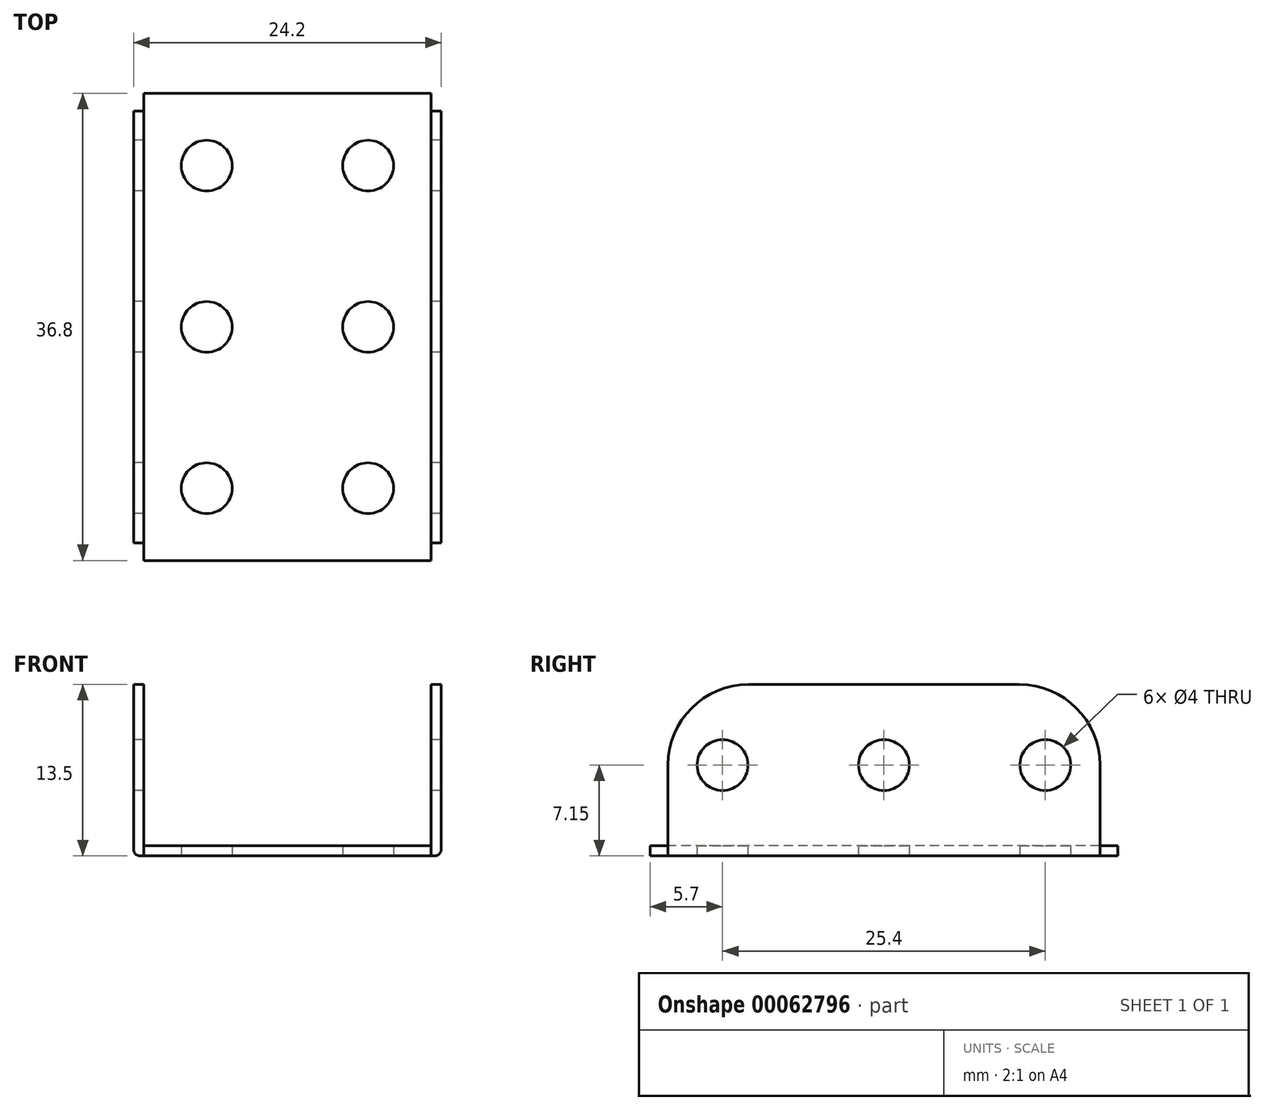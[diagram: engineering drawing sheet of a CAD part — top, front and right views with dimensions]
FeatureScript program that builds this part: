
annotation { "Feature Type Name" : "Feature", "Feature Type Description" : "" }
export const myFeature = defineFeature(function(context is Context, id is Id, definition is map)
    precondition{}
    {
        {
            var Q0;
            Q0=qCreatedBy(makeId("Top.planeOp"),FACE);
            var sketch = newSketch(context, id + "F0", { "sketchPlane" : qUnion([Q0])});
            skLineSegment(sketch, "E0.rect.bottom", {"start": v(11.3, 18.4) * mm, "end": v(-11.3, 18.4) * mm});
            skLineSegment(sketch, "E0.rect.top", {"start": v(11.3, -18.4) * mm, "end": v(-11.3, -18.4) * mm});
            skLineSegment(sketch, "E0.rect.left", {"start": v(11.3, 18.4) * mm, "end": v(11.3, -18.4) * mm});
            skLineSegment(sketch, "E0.rect.right", {"start": v(-11.3, 18.4) * mm, "end": v(-11.3, -18.4) * mm});
            skPoint(sketch, "E0.rect.middle", {"position": v(0, 0) * mm});
            skPoint(sketch, "E1", {"position": v(-6.35, -12.7) * mm});
            skCircle(sketch, "E2", {"center": v(-6.35, -12.7) * mm, "radius": 2 * mm});
            skCircle(sketch, "E3.0.1.0", {"center": v(-6.35, 0) * mm, "radius": 2 * mm});
            skCircle(sketch, "E3.0.2.0", {"center": v(-6.35, 12.7) * mm, "radius": 2 * mm});
            skCircle(sketch, "E3.1.0.0", {"center": v(6.35, -12.7) * mm, "radius": 2 * mm});
            skCircle(sketch, "E3.1.1.0", {"center": v(6.35, 0) * mm, "radius": 2 * mm});
            skCircle(sketch, "E3.1.2.0", {"center": v(6.35, 12.7) * mm, "radius": 2 * mm});
            skLineSegment(sketch, "E3.direction1", {"start": v(-6.35, -12.7) * mm, "end": v(6.35, -12.7) * mm, "construction": true});
            skLineSegment(sketch, "E3.direction2", {"start": v(-6.35, -12.7) * mm, "end": v(-6.35, 0) * mm, "construction": true});
            skLineSegment(sketch, "E4.rect.bottom", {"start": v(-11.3, 17) * mm, "end": v(-12.1, 17) * mm});
            skLineSegment(sketch, "E4.rect.top", {"start": v(-11.3, -17) * mm, "end": v(-12.1, -17) * mm});
            skLineSegment(sketch, "E4.rect.left", {"start": v(-11.3, 17) * mm, "end": v(-11.3, -17) * mm});
            skLineSegment(sketch, "E4.rect.right", {"start": v(-12.1, 17) * mm, "end": v(-12.1, -17) * mm});
            skPoint(sketch, "E4.rect.middle", {"position": v(-11.7, 0) * mm});
            skLineSegment(sketch, "E5.MirrorCS", {"start": v(12.1, 17) * mm, "end": v(12.1, -17) * mm});
            skLineSegment(sketch, "E6.MirrorCS", {"start": v(11.3, -17) * mm, "end": v(12.1, -17) * mm});
            skLineSegment(sketch, "E7.MirrorCS", {"start": v(11.3, 17) * mm, "end": v(12.1, 17) * mm});
            skSolve(sketch);
        }
        {
            var Q0;
            {var subQ0=sQuery(id+"F0.wireOp",EDGE,"E0.rect.bottom");Q0=makeQuery(id+"F0.imprint","IMPRINT",FACE,{"disambiguationData":[TD([[makeQuery(id+"F0.imprint","IMPRINT",EDGE,{"derivedFrom":subQ0}),1.0]])]});}
            var Q1;
            Q1=makeQuery(id+"F0.imprint","IMPRINT",FACE,{"disambiguationData":[TD([[makeQuery(id+"F0.imprint","IMPRINT",EDGE,{"derivedFrom":sQuery(id+"F0.wireOp",EDGE,"E5.MirrorCS")}),-1.0]])]});
            var Q2;
            Q2=makeQuery(id+"F0.imprint","IMPRINT",FACE,{"disambiguationData":[TD([[makeQuery(id+"F0.imprint","IMPRINT",EDGE,{"derivedFrom":sQuery(id+"F0.wireOp",EDGE,"E4.rect.bottom")}),1.0]])]});
            extrude(context, id + "F1", {"entities" : qUnion([Q0, Q1, Q2]), "depth" : 0.8 * mm});
        }
        {
            var Q0;
            Q0=makeQuery(id+"F1.opExtrude","CAP_FACE",FACE,{"disambiguationData":[OSD([sQuery(id+"F0.wireOp",EDGE,"E0.rect.bottom"),sQuery(id+"F0.wireOp",EDGE,"E0.rect.top"),sQuery(id+"F0.wireOp",EDGE,"E0.rect.left"),sQuery(id+"F0.wireOp",EDGE,"E0.rect.right"),sQuery(id+"F0.wireOp",EDGE,"E2"),sQuery(id+"F0.wireOp",EDGE,"E3.0.1.0"),sQuery(id+"F0.wireOp",EDGE,"E3.0.2.0"),sQuery(id+"F0.wireOp",EDGE,"E3.1.0.0"),sQuery(id+"F0.wireOp",EDGE,"E3.1.1.0"),sQuery(id+"F0.wireOp",EDGE,"E3.1.2.0"),sQuery(id+"F0.wireOp",EDGE,"E4.rect.bottom"),sQuery(id+"F0.wireOp",EDGE,"E4.rect.top"),sQuery(id+"F0.wireOp",EDGE,"E4.rect.right"),sQuery(id+"F0.wireOp",EDGE,"E5.MirrorCS"),sQuery(id+"F0.wireOp",EDGE,"E6.MirrorCS"),sQuery(id+"F0.wireOp",EDGE,"E7.MirrorCS")])],"isStart":false});
            var sketch = newSketch(context, id + "F2", { "sketchPlane" : qUnion([Q0])});
            skLineSegment(sketch, "E8", {"start": v(-11.3, 17) * mm, "end": v(-11.3, -17) * mm});
            skLineSegment(sketch, "E9", {"start": v(11.3, 17) * mm, "end": v(11.3, -17) * mm});
            skSolve(sketch);
        }
        {
            var Q0;
            Q0=makeQuery(id+"F2.imprint","IMPRINT",FACE,{"disambiguationData":[TD([[makeQuery(id+"F2.imprint","IMPRINT",EDGE,{"derivedFrom":sQuery(id+"F2.wireOp",EDGE,"E8")}),-1.0]])]});
            var Q1;
            Q1=makeQuery(id+"F2.imprint","IMPRINT",FACE,{"disambiguationData":[TD([[makeQuery(id+"F2.imprint","IMPRINT",EDGE,{"derivedFrom":sQuery(id+"F2.wireOp",EDGE,"E9")}),1.0]])]});
            extrude(context, id + "F3", {"entities" : qUnion([Q0, Q1]), "operationType" : NewBodyOperationType.ADD, "depth" : 12.7 * mm});
        }
        {
            var Q0;
            {var subQ0=sQuery(id+"F0.wireOp",EDGE,"E5.MirrorCS");Q0=makeQuery(id+"F3.boolean.opBoolean","MERGE",FACE,{"derivedFrom":[makeQuery(id+"F1.opExtrude","SWEPT_FACE",FACE,{"disambiguationData":[OSD([subQ0])]}),makeQuery(id+"F3.opExtrude","SWEPT_FACE",FACE,{"disambiguationData":[OSD([subQ0])]})]});}
            var sketch = newSketch(context, id + "F4", { "sketchPlane" : qUnion([Q0])});
            skPoint(sketch, "E10", {"position": v(-12.7, 7.15) * mm});
            skCircle(sketch, "E11", {"center": v(-12.7, 7.15) * mm, "radius": 2 * mm});
            skCircle(sketch, "E12.1.0.0", {"center": v(0, 7.15) * mm, "radius": 2 * mm});
            skCircle(sketch, "E12.2.0.0", {"center": v(12.7, 7.15) * mm, "radius": 2 * mm});
            skLineSegment(sketch, "E12.direction1", {"start": v(-12.7, 7.15) * mm, "end": v(0, 7.15) * mm, "construction": true});
            skSolve(sketch);
        }
        {
            var Q0;
            Q0=makeQuery(id+"F3.opExtrude","CAP_EDGE",EDGE,{"disambiguationData":[OSD([sQuery(id+"F0.wireOp",EDGE,"E7.MirrorCS")])],"isStart":false});
            var Q1;
            Q1=makeQuery(id+"F3.opExtrude","CAP_EDGE",EDGE,{"disambiguationData":[OSD([sQuery(id+"F0.wireOp",EDGE,"E4.rect.bottom")])],"isStart":false});
            var Q2;
            Q2=makeQuery(id+"F3.opExtrude","CAP_EDGE",EDGE,{"disambiguationData":[OSD([sQuery(id+"F0.wireOp",EDGE,"E6.MirrorCS")])],"isStart":false});
            var Q3;
            Q3=makeQuery(id+"F3.opExtrude","CAP_EDGE",EDGE,{"disambiguationData":[OSD([sQuery(id+"F0.wireOp",EDGE,"E4.rect.top")])],"isStart":false});
            fillet(context, id + "F5", {"entities" : qUnion([Q0, Q1, Q2, Q3]), "radius" : 6.35 * mm, "tangentPropagation" : true, "allowEdgeOverflow" : false});
        }
        {
            var Q0;
            Q0=sQuery(id+"F4.wireOp",VERTEX,"E10");
            var Q1;
            Q1=sQuery(id+"F4.wireOp",VERTEX,"E12.1.0.0.center");
            var Q2;
            Q2=sQuery(id+"F4.wireOp",VERTEX,"E12.2.0.0.center");
            var Q3;
            Q3=makeQuery(id+"F1.opExtrude","SWEPT_BODY",BODY,{"disambiguationData":[OSD([sQuery(id+"F0.wireOp",EDGE,"E0.rect.bottom"),sQuery(id+"F0.wireOp",EDGE,"E0.rect.top"),sQuery(id+"F0.wireOp",EDGE,"E0.rect.left"),sQuery(id+"F0.wireOp",EDGE,"E0.rect.right"),sQuery(id+"F0.wireOp",EDGE,"E2"),sQuery(id+"F0.wireOp",EDGE,"E3.0.1.0"),sQuery(id+"F0.wireOp",EDGE,"E3.0.2.0"),sQuery(id+"F0.wireOp",EDGE,"E3.1.0.0"),sQuery(id+"F0.wireOp",EDGE,"E3.1.1.0"),sQuery(id+"F0.wireOp",EDGE,"E3.1.2.0"),sQuery(id+"F0.wireOp",EDGE,"E4.rect.bottom"),sQuery(id+"F0.wireOp",EDGE,"E4.rect.top"),sQuery(id+"F0.wireOp",EDGE,"E4.rect.right"),sQuery(id+"F0.wireOp",EDGE,"E5.MirrorCS"),sQuery(id+"F0.wireOp",EDGE,"E6.MirrorCS"),sQuery(id+"F0.wireOp",EDGE,"E7.MirrorCS")])]});
            hole(context, id + "F6", {"style" : HoleStyle.SIMPLE, "holeDiameter" : 4 * mm, "endStyle" : HoleEndStyle.THROUGH, "locations" : qUnion([Q0, Q1, Q2]), "scope" : qUnion([Q3])});
        }
        {
            var Q0;
            Q0=makeQuery(id+"F1.opExtrude","CAP_EDGE",EDGE,{"disambiguationData":[OSD([sQuery(id+"F0.wireOp",EDGE,"E5.MirrorCS")])],"isStart":true});
            var Q1;
            Q1=makeQuery(id+"F1.opExtrude","CAP_EDGE",EDGE,{"disambiguationData":[OSD([sQuery(id+"F0.wireOp",EDGE,"E4.rect.right")])],"isStart":true});
            fillet(context, id + "F7", {"entities" : qUnion([Q0, Q1]), "radius" : 0.5 * mm, "tangentPropagation" : true, "allowEdgeOverflow" : false});
        }
    });
